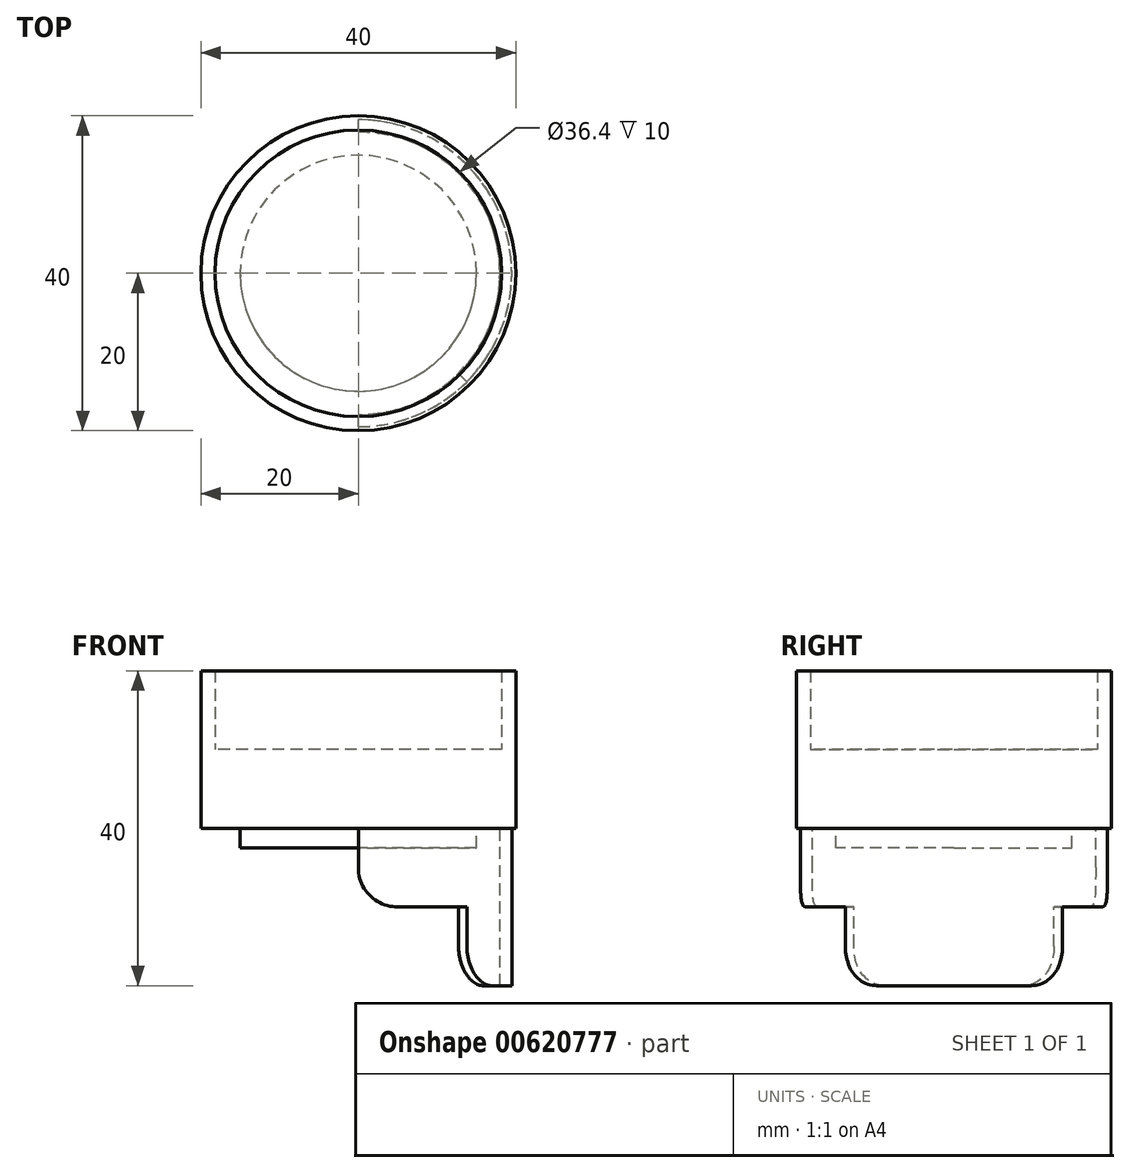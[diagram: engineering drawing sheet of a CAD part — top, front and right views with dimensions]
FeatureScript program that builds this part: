
annotation { "Feature Type Name" : "Feature", "Feature Type Description" : "" }
export const myFeature = defineFeature(function(context is Context, id is Id, definition is map)
    precondition{}
    {
        {
            var Q0;
            Q0=qCreatedBy(makeId("Top.planeOp"),FACE);
            var sketch = newSketch(context, id + "F0", { "sketchPlane" : qUnion([Q0])});
            skCircle(sketch, "E0", {"center": v(0, 0) * mm, "radius": 20 * mm});
            skSolve(sketch);
        }
        {
            var Q0;
            Q0=makeQuery(id+"F0.imprint","IMPRINT",FACE,{"disambiguationData":[TD([[makeQuery(id+"F0.imprint","IMPRINT",EDGE,{"derivedFrom":sQuery(id+"F0.wireOp",EDGE,"E0")}),1.0]])]});
            extrude(context, id + "F1", {"entities" : qUnion([Q0]), "depth" : 10 * mm, "offsetDistance" : 25 * mm});
        }
        {
            var Q0;
            Q0=makeQuery(id+"F1.opExtrude","CAP_FACE",FACE,{"disambiguationData":[OSD([sQuery(id+"F0.wireOp",EDGE,"E0")])],"isStart":false});
            var sketch = newSketch(context, id + "F2", { "sketchPlane" : qUnion([Q0])});
            skCircle(sketch, "E1.0", {"center": v(0, 0) * mm, "radius": 20 * mm});
            skCircle(sketch, "E2", {"center": v(0, 0) * mm, "radius": 18.2 * mm});
            skSolve(sketch);
        }
        {
            var Q0;
            Q0=makeQuery(id+"F2.imprint","IMPRINT",FACE,{"disambiguationData":[TD([[makeQuery(id+"F2.imprint","IMPRINT",EDGE,{"derivedFrom":sQuery(id+"F2.wireOp",EDGE,"E1.0")}),1.0]])]});
            extrude(context, id + "F3", {"entities" : qUnion([Q0]), "operationType" : NewBodyOperationType.ADD, "depth" : 10 * mm, "offsetDistance" : 25 * mm});
        }
        {
            var Q0;
            Q0=makeQuery(id+"F1.opExtrude","CAP_FACE",FACE,{"disambiguationData":[OSD([sQuery(id+"F0.wireOp",EDGE,"E0")])],"isStart":true});
            var sketch = newSketch(context, id + "F4", { "sketchPlane" : qUnion([Q0])});
            skCircle(sketch, "E3", {"center": v(0, 0) * mm, "radius": 19.5 * mm});
            skCircle(sketch, "E4", {"center": v(0, 0) * mm, "radius": 18 * mm});
            skLineSegment(sketch, "E5", {"start": v(0, 20) * mm, "end": v(0, 18) * mm});
            skLineSegment(sketch, "E6", {"start": v(0, -18) * mm, "end": v(0, -20) * mm});
            skLineSegment(sketch, "E7", {"start": v(14.14, 14.14) * mm, "end": v(0, 0) * mm});
            skLineSegment(sketch, "E8", {"start": v(0, 0) * mm, "end": v(14.14, -14.14) * mm});
            skCircle(sketch, "E9", {"center": v(0, 0) * mm, "radius": 15 * mm});
            skSolve(sketch);
        }
        {
            var Q0;
            {var subQ0=sQuery(id+"F4.wireOp",EDGE,"E7");var subQ1=sQuery(id+"F4.wireOp",EDGE,"E3");var subQ2=makeQuery(id+"F4.imprint","INTERSECT",VERTEX,{"derivedFrom":[subQ1,subQ0]});Q0=makeQuery(id+"F4.imprint","IMPRINT",FACE,{"disambiguationData":[TD([[makeQuery(id+"F4.imprint","IMPRINT",EDGE,{"disambiguationData":[TD([[subQ2,1.0]])],"derivedFrom":subQ1}),1.0]])]});}
            extrude(context, id + "F5", {"entities" : qUnion([Q0]), "operationType" : NewBodyOperationType.ADD, "depth" : 20 * mm, "offsetDistance" : 25 * mm});
        }
        {
            var Q0;
            {var subQ0=sQuery(id+"F4.wireOp",EDGE,"E6");var subQ1=sQuery(id+"F4.wireOp",EDGE,"E3");var subQ2=makeQuery(id+"F4.imprint","INTERSECT",VERTEX,{"derivedFrom":[subQ1,subQ0]});Q0=makeQuery(id+"F4.imprint","IMPRINT",FACE,{"disambiguationData":[TD([[makeQuery(id+"F4.imprint","IMPRINT",EDGE,{"disambiguationData":[TD([[subQ2,-1.0]])],"derivedFrom":subQ1}),1.0]])]});}
            var Q1;
            {var subQ0=sQuery(id+"F4.wireOp",EDGE,"E5");var subQ1=sQuery(id+"F4.wireOp",EDGE,"E3");var subQ2=makeQuery(id+"F4.imprint","INTERSECT",VERTEX,{"derivedFrom":[subQ1,subQ0]});Q1=makeQuery(id+"F4.imprint","IMPRINT",FACE,{"disambiguationData":[TD([[makeQuery(id+"F4.imprint","IMPRINT",EDGE,{"disambiguationData":[TD([[subQ2,1.0]])],"derivedFrom":subQ1}),1.0]])]});}
            extrude(context, id + "F6", {"entities" : qUnion([Q0, Q1]), "operationType" : NewBodyOperationType.ADD, "depth" : 10 * mm, "offsetDistance" : 25 * mm});
        }
        {
            var Q0;
            Q0=makeQuery(id+"F6.opExtrude","CAP_EDGE",EDGE,{"disambiguationData":[OSD([sQuery(id+"F4.wireOp",EDGE,"E6")])],"isStart":false});
            var Q1;
            Q1=makeQuery(id+"F6.opExtrude","CAP_EDGE",EDGE,{"disambiguationData":[OSD([sQuery(id+"F4.wireOp",EDGE,"E8")])],"isStart":false});
            var Q2;
            Q2=makeQuery(id+"F5.opExtrude","CAP_EDGE",EDGE,{"disambiguationData":[OSD([sQuery(id+"F4.wireOp",EDGE,"E8")])],"isStart":false});
            var Q3;
            Q3=makeQuery(id+"F5.opExtrude","CAP_EDGE",EDGE,{"disambiguationData":[OSD([sQuery(id+"F4.wireOp",EDGE,"E7")])],"isStart":false});
            var Q4;
            Q4=makeQuery(id+"F6.opExtrude","CAP_EDGE",EDGE,{"disambiguationData":[OSD([sQuery(id+"F4.wireOp",EDGE,"E7")])],"isStart":false});
            var Q5;
            Q5=makeQuery(id+"F6.opExtrude","CAP_EDGE",EDGE,{"disambiguationData":[OSD([sQuery(id+"F4.wireOp",EDGE,"E5")])],"isStart":false});
            fillet(context, id + "F7", {"entities" : qUnion([Q0, Q1, Q2, Q3, Q4, Q5]), "radius" : 5 * mm, "tangentPropagation" : true, "allowEdgeOverflow" : false});
        }
        {
            var Q0;
            {var subQ0=sQuery(id+"F4.wireOp",EDGE,"E8");var subQ1=sQuery(id+"F4.wireOp",EDGE,"E7");var subQ2=makeQuery(id+"F4.imprint","INTERSECT",VERTEX,{"derivedFrom":[subQ1,subQ0]});Q0=makeQuery(id+"F4.imprint","IMPRINT",FACE,{"disambiguationData":[TD([[makeQuery(id+"F4.imprint","IMPRINT",EDGE,{"disambiguationData":[TD([[subQ2,1.0]])],"derivedFrom":subQ1}),-1.0]])]});}
            var Q1;
            {var subQ0=sQuery(id+"F4.wireOp",EDGE,"E8");var subQ1=sQuery(id+"F4.wireOp",EDGE,"E7");var subQ2=makeQuery(id+"F4.imprint","INTERSECT",VERTEX,{"derivedFrom":[subQ1,subQ0]});Q1=makeQuery(id+"F4.imprint","IMPRINT",FACE,{"disambiguationData":[TD([[makeQuery(id+"F4.imprint","IMPRINT",EDGE,{"disambiguationData":[TD([[subQ2,1.0]])],"derivedFrom":subQ1}),1.0]])]});}
            extrude(context, id + "F8", {"entities" : qUnion([Q0, Q1]), "operationType" : NewBodyOperationType.ADD, "depth" : 2.5 * mm, "offsetDistance" : 25 * mm});
        }
    });
